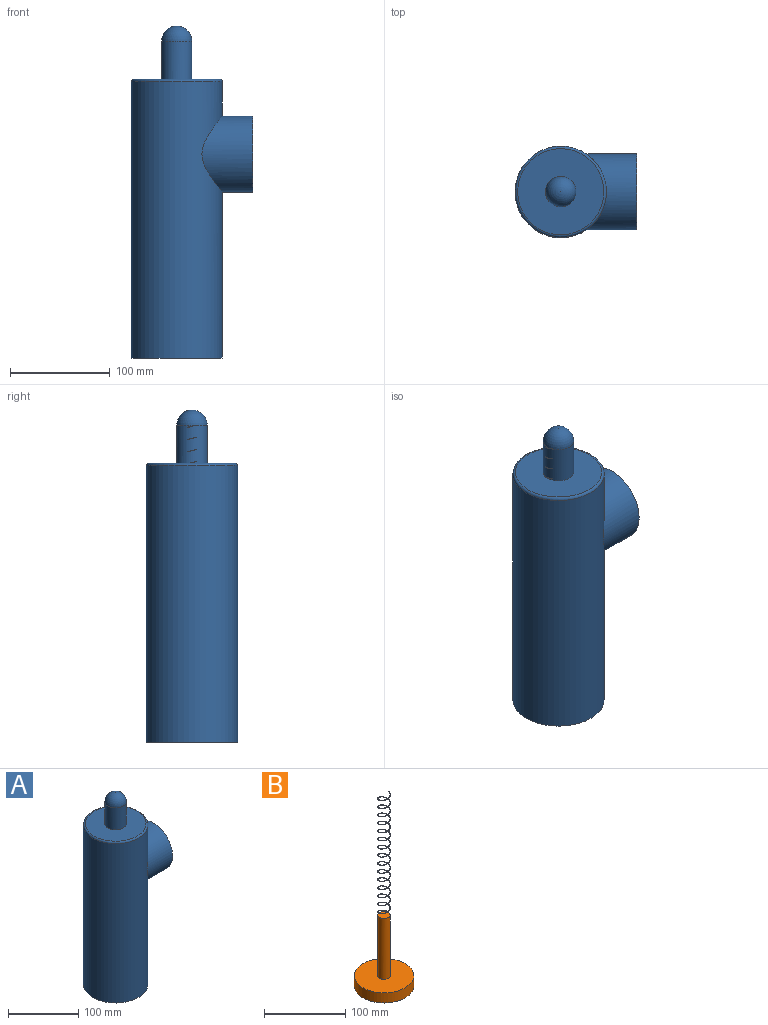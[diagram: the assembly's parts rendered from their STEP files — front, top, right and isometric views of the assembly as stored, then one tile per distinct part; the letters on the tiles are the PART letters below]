
ASSEMBLY  parts=2 mates=1
PART A: 17 faces, bbox 125.7x99x332.7 mm
  f0: cylinder r=30.48mm len=60.96mm, axis (1,0,0), area 7592.9mm2, adj f7,f8
  f1: cylinder r=45.72mm len=276.86mm, axis (0,0,-1), area 74404.4mm2, adj f3,f6,f13
  f2: plane 86.36x86.36mm, normal (0,0,1), area 5127.9mm2, adj f4,f13
  f3: plane 91.44x91.44mm, normal (0,0,-1), area 846.4mm2, adj f1,f14
  f4: cylinder r=15.24mm len=38.1mm, axis (0,0,-1), area 3648.3mm2, adj f2,f5
  f5: sphere r=15.24mm, area 1459.8mm2, adj f4
  f6: cylinder r=38.1mm len=76.2mm, axis (-1,0,0), area 9566.7mm2, adj f1,f7
  f7: plane 76.2x76.2mm, normal (1,0,0), area 1641.7mm2, adj f0,f6
  f8: cylinder r=42.67mm len=76.2mm, axis (0,0,-1), area 2111.5mm2, adj f0,f12
  f9: plane 86.36x86.36mm, normal (0,0,-1), area 5390.6mm2, adj f11,f15
  f10: plane 86.36x86.36mm, normal (0,0,1), area 137mm2, adj f11,f14
  f11: cylinder r=43.18mm len=274.32mm, axis (0,0,-1), area 69180.4mm2, adj f9,f10,f12
  f12: cylinder r=38.1mm len=76.2mm, axis (-1,0,0), area 173.1mm2, adj f8,f11
  f13: torus R=43.18mm, axis (0,0,1), area 1123mm2, adj f1,f2
  f14: cylinder r=42.67mm len=85.34mm, axis (0,0,-1), area 681mm2, adj f3,f10
  f15: cylinder r=12.19mm len=45.72mm, axis (0,0,-1), area 3502.4mm2, adj f9,f16
  f16: plane 24.38x24.38mm, normal (0,0,-1), area 467mm2, adj f15
PART B: 8 faces, bbox 73.2x73.2x289.6 mm
  f0: cylinder r=36.58mm len=73.15mm, axis (0,0,-1), area 3502.4mm2, adj f1,f2
  f1: plane 73.15x73.15mm, normal (0,0,1), area 4020.4mm2, adj f0,f3
  f2: plane 73.15x73.15mm, normal (0,0,-1), area 4202.8mm2, adj f0
  f3: cylinder r=7.62mm len=91.44mm, axis (0,0,-1), area 4378mm2, adj f1,f4,f5
  f4: plane 15.28x15.28mm, normal (0,0,1), area 182.4mm2, adj f3,f7
  f5: plane 0.31x0.18mm, normal (0,0,-1), area 0mm2, adj f3,f7
  f6: plane 0.31x0.31mm, normal (0,0,1), area 0.1mm2, adj f7
  f7: bspline ~182.88x15.74mm, area 433.4mm2, adj f4,f5,f6
PLACE A t=(50.35,-5.22,-59.44)mm
PLACE B t=(42.73,-5.22,-26.42)mm
MATE fastened B.f6 <-> A.f15  axis (0,0,1) through (50.35,-5.22,263.14)mm
